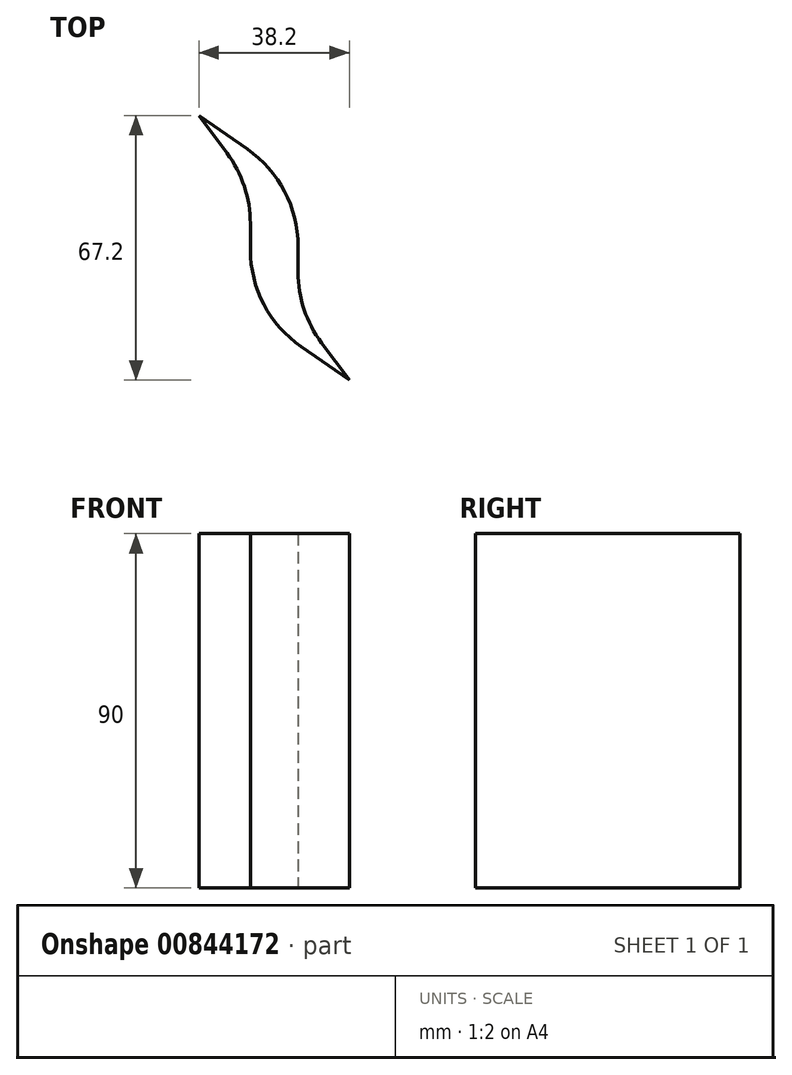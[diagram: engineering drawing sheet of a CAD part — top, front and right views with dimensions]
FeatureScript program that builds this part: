
annotation { "Feature Type Name" : "Feature", "Feature Type Description" : "" }
export const myFeature = defineFeature(function(context is Context, id is Id, definition is map)
    precondition{}
    {
        {
            var Q0;
            Q0=qCreatedBy(makeId("Top.planeOp"),FACE);
            var sketch = newSketch(context, id + "F0", { "sketchPlane" : qUnion([Q0])});
            skPoint(sketch, "E0.middle", {"position": v(0, 0) * mm});
            skLineSegment(sketch, "E1.left", {"start": v(6.07, 0.44) * mm, "end": v(6.07, -6.18) * mm});
            skLineSegment(sketch, "E1.right", {"start": v(-6.07, 6.18) * mm, "end": v(-6.07, -0.44) * mm});
            skLineSegment(sketch, "E2", {"start": v(-12.02, 24.11) * mm, "end": v(-19.1, 33.6) * mm});
            skLineSegment(sketch, "E3", {"start": v(-6.82, 25.08) * mm, "end": v(-19.1, 33.6) * mm});
            skLineSegment(sketch, "E4", {"start": v(6.82, -25.08) * mm, "end": v(19.1, -33.6) * mm});
            skLineSegment(sketch, "E5", {"start": v(12.02, -24.11) * mm, "end": v(19.1, -33.6) * mm});
            skPoint(sketch, "E6.visualSharp", {"position": v(-6.07, 16.13) * mm});
            skArc(sketch, "E6.filletArc", {"start": v(-6.07, 6.18) * mm, "mid": v(-7.6, 15.63) * mm, "end": v(-12.02, 24.11) * mm});
            skPoint(sketch, "E7.visualSharp", {"position": v(-6.07, -16.13) * mm});
            skArc(sketch, "E7.filletArc", {"start": v(-6.07, -0.44) * mm, "mid": v(-2.65, -14.35) * mm, "end": v(6.82, -25.08) * mm});
            skPoint(sketch, "E8.visualSharp", {"position": v(6.07, -16.13) * mm});
            skArc(sketch, "E8.filletArc", {"start": v(6.07, -6.18) * mm, "mid": v(7.6, -15.63) * mm, "end": v(12.02, -24.11) * mm});
            skPoint(sketch, "E9.visualSharp", {"position": v(6.07, 16.13) * mm});
            skArc(sketch, "E9.filletArc", {"start": v(6.07, 0.44) * mm, "mid": v(2.65, 14.35) * mm, "end": v(-6.82, 25.08) * mm});
            skPoint(sketch, "E0.left.end.orphan", {"position": v(19.1, 33.6) * mm});
            skPoint(sketch, "E0.right.start.orphan", {"position": v(-19.1, -33.6) * mm});
            skSolve(sketch);
        }
        {
            var Q0;
            Q0 = qSketchRegion(id + "F0", true);
            extrude(context, id + "F1", {"entities" : qUnion([Q0]), "depth" : 90 * mm, "offsetDistance" : 25 * mm});
        }
    });
